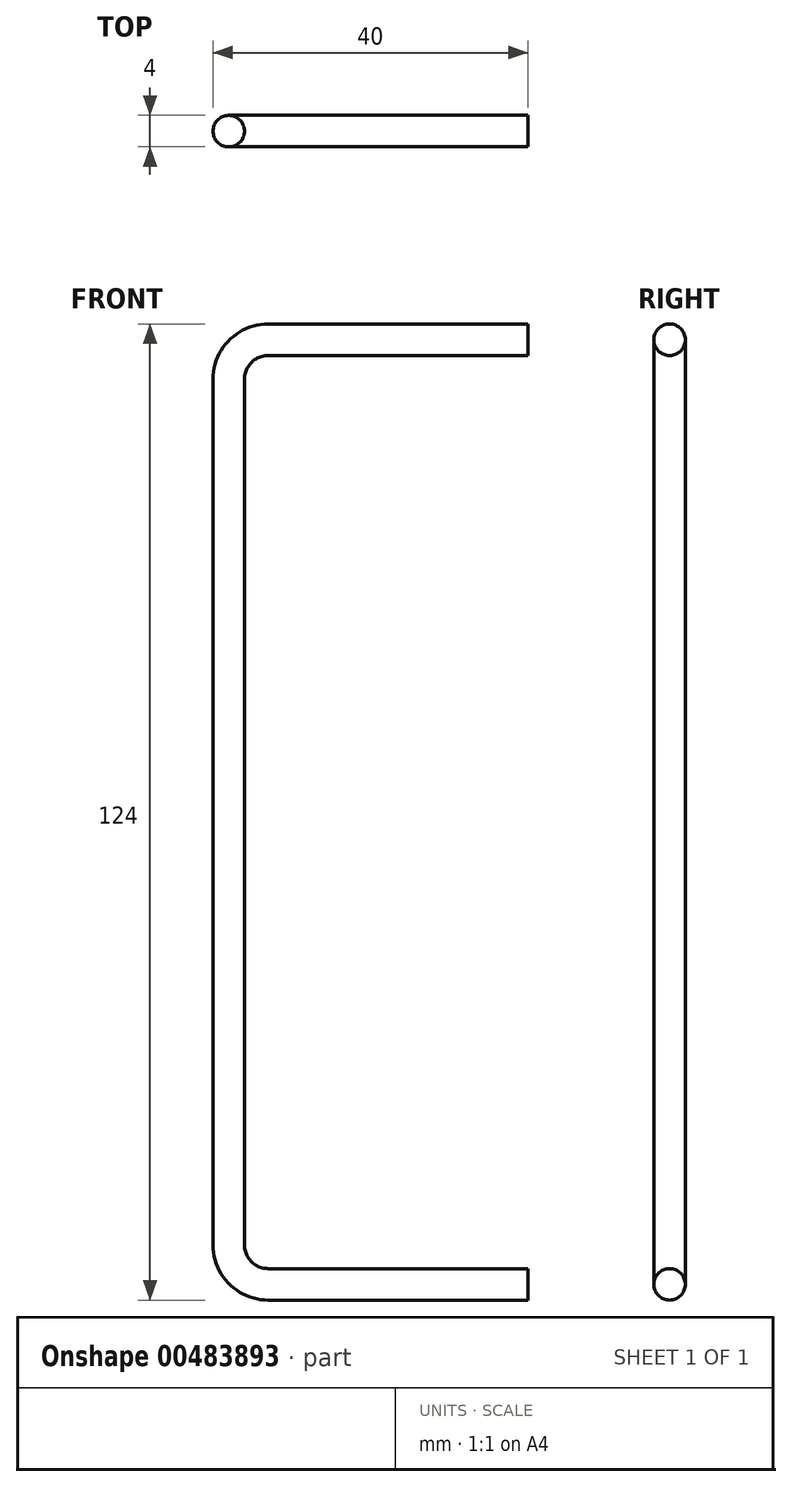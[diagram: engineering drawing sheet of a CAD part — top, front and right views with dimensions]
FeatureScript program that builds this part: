
annotation { "Feature Type Name" : "Feature", "Feature Type Description" : "" }
export const myFeature = defineFeature(function(context is Context, id is Id, definition is map)
    precondition{}
    {
        {
            var Q0;
            Q0=qCreatedBy(makeId("Front.planeOp"),FACE);
            var sketch = newSketch(context, id + "F0", { "sketchPlane" : qUnion([Q0])});
            skLineSegment(sketch, "E0", {"start": v(0, 0) * mm, "end": v(-33, 0) * mm});
            skLineSegment(sketch, "E1", {"start": v(-38, 5) * mm, "end": v(-38, 115) * mm});
            skLineSegment(sketch, "E2", {"start": v(-33, 120) * mm, "end": v(0, 120) * mm});
            skPoint(sketch, "E3.visualSharp", {"position": v(-38, 120) * mm});
            skArc(sketch, "E3.filletArc", {"start": v(-33, 120) * mm, "mid": v(-36.54, 118.54) * mm, "end": v(-38, 115) * mm});
            skPoint(sketch, "E4.visualSharp", {"position": v(-38, 0) * mm});
            skArc(sketch, "E4.filletArc", {"start": v(-38, 5) * mm, "mid": v(-36.54, 1.46) * mm, "end": v(-33, 0) * mm});
            skSolve(sketch);
        }
        {
            var Q0;
            Q0=qCreatedBy(makeId("Right.planeOp"),FACE);
            var sketch = newSketch(context, id + "F1", { "sketchPlane" : qUnion([Q0])});
            skCircle(sketch, "E5", {"center": v(0, 0) * mm, "radius": 2 * mm});
            skSolve(sketch);
        }
        {
            var Q0;
            Q0 = qSketchRegion(id + "F1", true);
            var Q1;
            Q1 = qConstructionFilter(qBodyType(qCreatedBy(id + "F0" ,EDGE), BodyType.WIRE), ConstructionObject.NO);
            sweep(context, id + "F2", {"profiles" : qUnion([Q0]), "path" : qUnion([Q1])});
        }
    });
